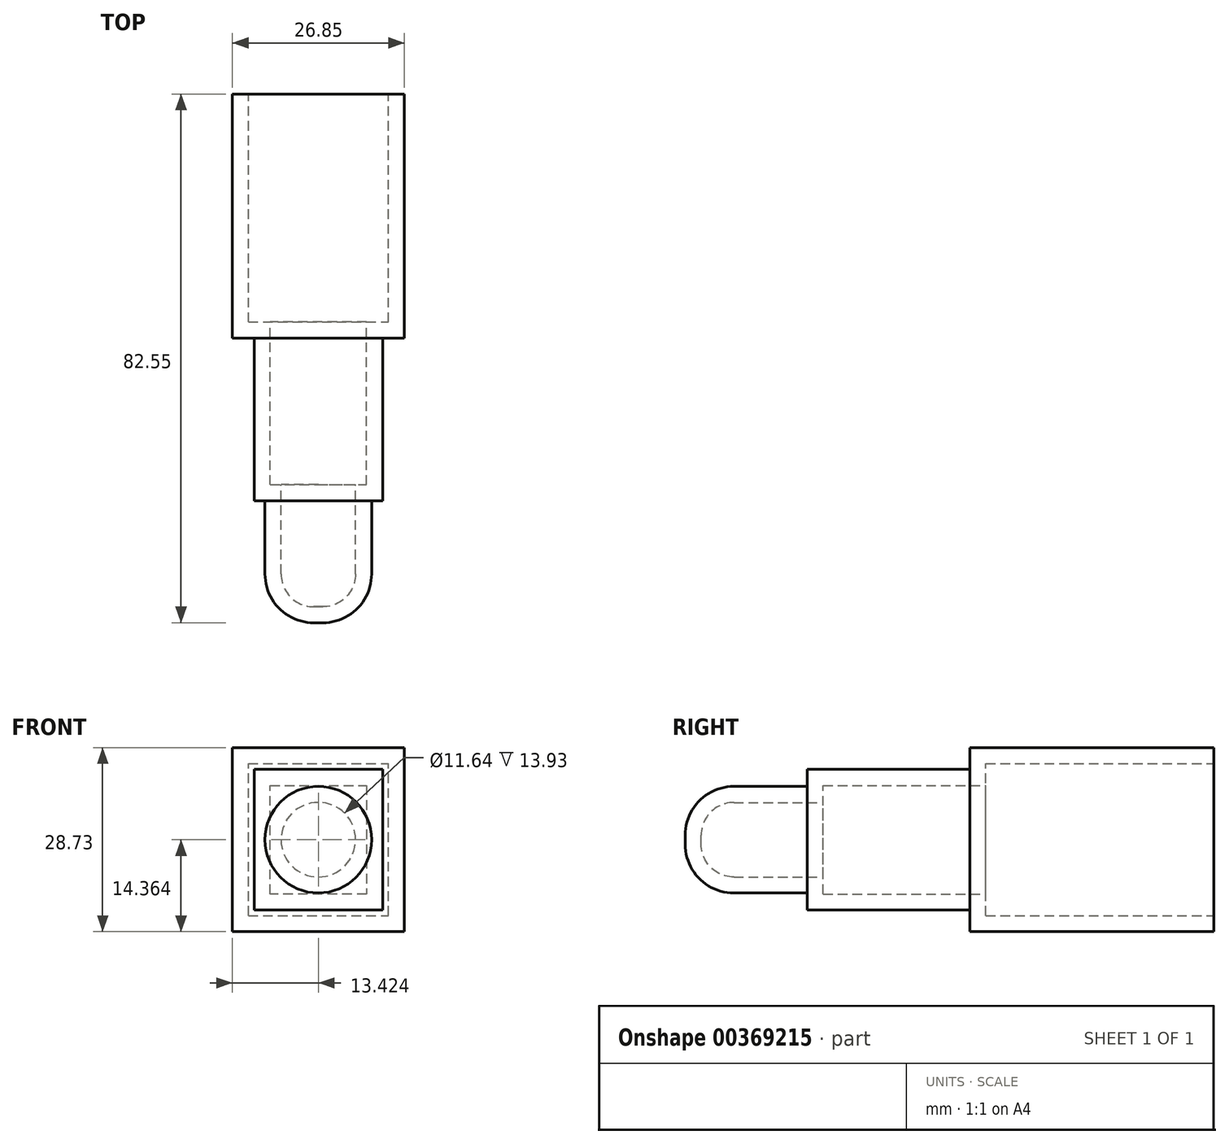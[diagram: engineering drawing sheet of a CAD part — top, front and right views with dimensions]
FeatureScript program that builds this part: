
annotation { "Feature Type Name" : "Feature", "Feature Type Description" : "" }
export const myFeature = defineFeature(function(context is Context, id is Id, definition is map)
    precondition{}
    {
        {
            var Q0;
            Q0=qCreatedBy(makeId("Front.planeOp"),FACE);
            var sketch = newSketch(context, id + "F0", { "sketchPlane" : qUnion([Q0])});
            skLineSegment(sketch, "E0.bottom", {"start": v(0, 0) * mm, "end": v(26.85, 0) * mm});
            skLineSegment(sketch, "E0.top", {"start": v(0, 28.73) * mm, "end": v(26.85, 28.73) * mm});
            skLineSegment(sketch, "E0.left", {"start": v(0, 0) * mm, "end": v(0, 28.73) * mm});
            skLineSegment(sketch, "E0.right", {"start": v(26.85, 0) * mm, "end": v(26.85, 28.73) * mm});
            skSolve(sketch);
        }
        {
            var Q0;
            Q0=makeQuery(id+"F0.imprint","IMPRINT",FACE,{"disambiguationData":[TD([[makeQuery(id+"F0.imprint","IMPRINT",EDGE,{"derivedFrom":sQuery(id+"F0.wireOp",EDGE,"E0.bottom")}),1.0]])]});
            extrude(context, id + "F1", {"entities" : qUnion([Q0]), "depth" : 38.1 * mm});
        }
        {
            var Q0;
            Q0=makeQuery(id+"F1.opExtrude","CAP_FACE",FACE,{"disambiguationData":[OSD([sQuery(id+"F0.wireOp",EDGE,"E0.bottom"),sQuery(id+"F0.wireOp",EDGE,"E0.top"),sQuery(id+"F0.wireOp",EDGE,"E0.left"),sQuery(id+"F0.wireOp",EDGE,"E0.right")])],"isStart":false});
            var sketch = newSketch(context, id + "F2", { "sketchPlane" : qUnion([Q0])});
            skLineSegment(sketch, "E1", {"start": v(0, 0) * mm, "end": v(0, 28.73) * mm});
            skLineSegment(sketch, "E2", {"start": v(0, 28.73) * mm, "end": v(26.85, 28.73) * mm});
            skLineSegment(sketch, "E3", {"start": v(26.85, 28.73) * mm, "end": v(26.85, 0) * mm});
            skLineSegment(sketch, "E4", {"start": v(26.85, 0) * mm, "end": v(0, 0) * mm});
            skPoint(sketch, "E5.endSnap0", {"position": v(13.42, 28.73) * mm});
            skLineSegment(sketch, "E6.0", {"start": v(3.4, 25.34) * mm, "end": v(23.46, 25.34) * mm});
            skLineSegment(sketch, "E6.1", {"start": v(3.4, 3.4) * mm, "end": v(3.4, 25.34) * mm});
            skLineSegment(sketch, "E6.2", {"start": v(23.46, 3.4) * mm, "end": v(3.4, 3.4) * mm});
            skLineSegment(sketch, "E6.3", {"start": v(23.46, 25.34) * mm, "end": v(23.46, 3.4) * mm});
            skSolve(sketch);
        }
        {
            var Q0;
            Q0=makeQuery(id+"F2.imprint","IMPRINT",FACE,{"disambiguationData":[TD([[makeQuery(id+"F2.imprint","IMPRINT",EDGE,{"derivedFrom":sQuery(id+"F2.wireOp",EDGE,"E6.0")}),-1.0]])]});
            extrude(context, id + "F3", {"entities" : qUnion([Q0]), "operationType" : NewBodyOperationType.ADD, "depth" : 25.4 * mm});
        }
        {
            var Q0;
            Q0=makeQuery(id+"F3.opExtrude","CAP_FACE",FACE,{"disambiguationData":[OSD([sQuery(id+"F2.wireOp",EDGE,"E6.0"),sQuery(id+"F2.wireOp",EDGE,"E6.1"),sQuery(id+"F2.wireOp",EDGE,"E6.2"),sQuery(id+"F2.wireOp",EDGE,"E6.3")])],"isStart":false});
            var sketch = newSketch(context, id + "F4", { "sketchPlane" : qUnion([Q0])});
            skLineSegment(sketch, "E7.bottom", {"start": v(3.4, 3.4) * mm, "end": v(23.46, 3.4) * mm});
            skLineSegment(sketch, "E7.top", {"start": v(3.4, 25.34) * mm, "end": v(23.46, 25.34) * mm});
            skLineSegment(sketch, "E7.left", {"start": v(3.4, 3.4) * mm, "end": v(3.4, 25.34) * mm});
            skLineSegment(sketch, "E7.right", {"start": v(23.46, 3.4) * mm, "end": v(23.46, 25.34) * mm});
            skLineSegment(sketch, "E8", {"start": v(13.42, 25.34) * mm, "end": v(13.42, 14.36) * mm});
            skPoint(sketch, "E8.endSnap0", {"position": v(3.4, 14.36) * mm});
            skCircle(sketch, "E9", {"center": v(13.42, 14.36) * mm, "radius": 8.32 * mm});
            skSolve(sketch);
        }
        {
            var Q0;
            Q0=makeQuery(id+"F4.imprint","IMPRINT",FACE,{"disambiguationData":[TD([[makeQuery(id+"F4.imprint","IMPRINT",EDGE,{"derivedFrom":sQuery(id+"F4.wireOp",EDGE,"E9")}),1.0]])]});
            extrude(context, id + "F5", {"entities" : qUnion([Q0]), "operationType" : NewBodyOperationType.ADD, "depth" : 19.05 * mm});
        }
        {
            var Q0;
            Q0=makeQuery(id+"F5.opExtrude","CAP_EDGE",EDGE,{"disambiguationData":[OSD([sQuery(id+"F4.wireOp",EDGE,"E9")])],"isStart":false});
            fillet(context, id + "F6", {"entities" : qUnion([Q0]), "radius" : 7.62 * mm, "tangentPropagation" : true, "allowEdgeOverflow" : false});
        }
        {
            var Q0;
            Q0=makeQuery(id+"F1.opExtrude","CAP_FACE",FACE,{"disambiguationData":[OSD([sQuery(id+"F0.wireOp",EDGE,"E0.bottom"),sQuery(id+"F0.wireOp",EDGE,"E0.top"),sQuery(id+"F0.wireOp",EDGE,"E0.left"),sQuery(id+"F0.wireOp",EDGE,"E0.right")])],"isStart":true});
            shell(context, id + "F7", {"entities" : qUnion([Q0]), "thickness" : 2.5 * mm});
        }
    });
